# Revit family: STS-1
name_source: partatom
category: Plumbing Fixtures
revit_build: Autodesk Revit MEP 2016 (Build: 20150220_1215(x64)
units: mm (PartAtom-declared; Revit-internal decimal feet)

## family parameters
Cut with Voids When Loaded = No
Host = Face
OmniClass Number = 23.65.00.00
OmniClass Title = Supply and Distribution of Liquids and Gases
Part Type = Normal
Room Calculation Point = No
Round Connector Dimension = Use Diameter
Shared = Yes

## types (1)
- STS-1
    Assembly Code = D2020
    Booster Pump- Manufacturer and Model Number = No
    CW Connection = No
    CWFU = 0
    Default Elevation = 0"
    Description = Emergency  Water Tempering Skid System
    HW Connection = Yes
    HWFU = 0
    Manufacturer = Acorn Controls
    Material = Stainless Steel
    Model = STS-1
    NEMA 7 Class Components           Division1            Division2 = No
    Recirculation Pump- = Yes
    Revised Date = 04/2/2018
    STS-1- 120 Gallon NON ASME Tank (Standard) With  ET71-2 Tempering Valve = Yes
    STS-1A- 120 Gallon ASME Tank With  ET71-2 Tempering Valve = No
    STS-3- 300 Gallon ASME Tank With  ET71-3 Tempering Valve = No
    Tempered Water Connection = No
    URL = http://www.acorneng.com
    Vent Connection = No
    WFU = 0
    Waste Connection = No

## geometry (parser evidence)
native form markers: Sweep x3
no freeform markers — native parametric forms only
